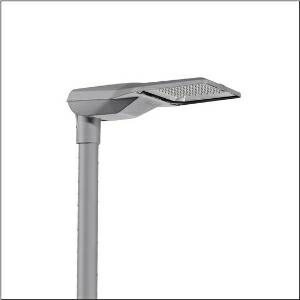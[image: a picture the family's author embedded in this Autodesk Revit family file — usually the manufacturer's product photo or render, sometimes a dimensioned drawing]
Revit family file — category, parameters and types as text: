
# Revit family: streetlight_sl_21_iq_midi___st1_0a_5xe3d21d08nb_d513
name_source: partatom
category: Lighting Fixtures
units: mm (PartAtom-declared; Revit-internal decimal feet)

## family parameters
Cut with Voids When Loaded = No
Host = Face
Light Source = No
Part Type = Normal
Room Calculation Point = No
Round Connector Dimension = Use Diameter
Shared = No

## types (1)
- --- (1 x LED, 19210 lm, 155.5 W, 2200K)
    Apparent Load = 155 VA
    CIE Flux Codes = 40 73 97 100 100
    Color Rendering = 70
    Color Temperature = 2200K
    Default Elevation = 1800 mm
    Description = Streetlight SL 21 iQ midi, mast luminaire, primary light control with lens, of PMMA, primary optical cover: cover, of toughened safety glass, transparent, light distribution: ST1.0a, light emission: direct distribution, primary light characteristic: asymmetric, installation type: post-top, side-entry, LED, High Power LED, rated luminous flux: 19.210lm, luminous efficacy: 124lm/W, light colour: 722, colour temperature: 2200K, control gear: iQ-Comfort, control: Auto-Match, Temp-Guard, Lumen-Switch, Night-Set, Smart-Wire, Light-Fading, Desk-Remote (wireless, voltage-free reading and setting of iQ features in the workshop via application-optimized NFC function/RFID function), optimised constant luminous flux control (CLO 2.0), pre-setting: linear dimming characteristic, mains connection: 230..240V, AC, 50/60Hz, start of lifetime: 156W, end of service life: 162W, reduction: 69W, luminaire housing, of diecast aluminium, powder-coated, Siteco® metallic grey (DB 702S), corrosivity category C5 mid according to DIN EN ISO 12944, please order mast flange separately, inclination adjustable: 0°, 5°, 10°, 15°, sealing non-destructively replaceable, multi-level sealing system, length: 644mm, width: 335mm, height: 110mm, mast flange for spigot size: 42mm (side-entry): 5XC10008XM4, 60/48mm (side-entry/post-top): 5XC10108XM2, 76/60mm (side-entry/post-top): 5XC10108XM1, mounting height: 4..8m, protection rating (complete): IP66, insulation class (complete): insulation class II (safety insulation), certification: CE, ENEC, ENEC+, VDE, impact resistance: IK10, permissible operating ambient temperature for outdoor applications: -40..+50°C, standard-compliant lighting for roads and squares, packaging unit: 1 piece

Light Distribution: ST1.0a
    Height = 111 mm
    Lamp = 1 x LED
    Lamp Light Flux = 19210 lm
    Lamp Power = 155.5 W
    Lamp count = 1
    Length = 644 mm
    Luminous efficacy = 124 lm/W
    Manufacturer = Siteco
    ModVariant = No
    Model = 5XE3D21D08NB
    Number of Poles = 1
    OnlyDefault = Yes
    Power Factor = 1
    Product Name = Streetlight SL 21 iQ midi | ST1.0a
    Product group = mast luminaire | pylon top
    ProductGroupID = 6100
    Protection Class = Protection class II
    Protection Degree = IP 66
    RLX_Detail_Level = 1
    RLX_Emergency_Light_Flux = 0 lm
    RLX_Emergency_Type = 0
    RLX_Emergency_Type_DB = No
    RlxData = <blob elided: 27237 chars, md5=773b708b>
    Socket = socket
    Standby Power = 0 W
    System Light Flux = 19210 lm
    System Power = 155 W
    Type Comments = factory setting: luminous flux: 100 % | dim-lin: 254 | 823 mA
    Type Image = l_1004298.jpg
    URL = http://relux.com
    VarID = @adj_170970
    Voltage = 0 V
    Weight = 0.00 kg
    Width = 336 mm

## geometry (parser evidence)
native form markers: Blend x4, Sweep x11
no freeform markers — native parametric forms only
